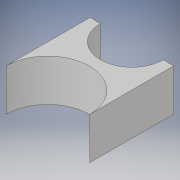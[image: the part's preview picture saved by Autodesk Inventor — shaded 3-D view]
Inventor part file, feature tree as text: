
AUTODESK INVENTOR PART (.ipt)
format: ipt  version: 2019 (Build 230136000, 136)  size: 115,712 bytes
history: native  units: mm
features: sketch x3, hole x2, other x1, extrude x1
ambient origin geometry x8: Origin, YZ Plane, XZ Plane, XY Plane, X Axis, Y Axis, Z Axis, Center Point
bodies: Body1 (feature_tree)
feature tree (7):
  other  "ソリッド1"
  extrude  "押し出し1"  Depth=40.0mm
  hole  "穴1"  [1 undecoded]
  hole  "穴2"  [1 undecoded]
  sketch  "スケッチ1"
  sketch  "スケッチ2"
  sketch  "スケッチ3"
note: 2 required parameter values undecoded (feature->parameter linkage not recoverable at this tier; creation-order binding heuristic only, values carry confidence <= 0.55)
